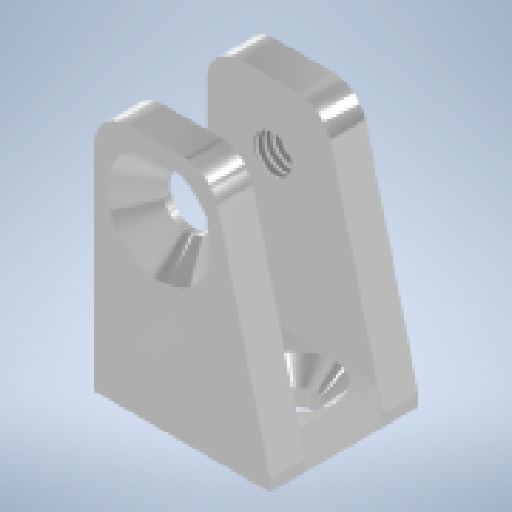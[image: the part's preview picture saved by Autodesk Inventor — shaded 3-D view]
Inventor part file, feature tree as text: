
AUTODESK INVENTOR PART (.ipt)
format: ipt  version: 2025 (Build 290162010, 162A)  size: 224,768 bytes
history: native  units: mm
features: sketch x5, hole x3, extrude x2, chamfer x2, fillet x1
ambient origin geometry x8: Origin, YZ Plane, XZ Plane, XY Plane, X Axis, Y Axis, Z Axis, Center Point
bodies: Volumenkörper1 (feature_tree)
feature tree (13):
  extrude  "Extrusion1"  Depth=3.0mm
  chamfer  "Fasen1"  Distance=21.0mm
  chamfer  "Fasen2"  Distance=20.0mm
  fillet  "Rundung1"  Radius=5.0mm
  hole  "Bohrung1"  [1 undecoded]
  extrude  "Extrusion2"  Depth=8.0mm
  hole  "Bohrung2"  [1 undecoded]
  hole  "Bohrung3"  [1 undecoded]
  sketch  "Skizze1"  dims[d0=15.0mm d1=3.0mm]
  sketch  "Skizze2"  dims[d2=3.0mm]
  sketch  "Skizze3"  dims[d3=6.6mm d5=21.0mm d6=0.0mm]
  sketch  "Skizze4"  dims[d7=3.0mm]
  sketch  "Skizze5"  dims[d8=3.242mm d9=8.0mm d10=9.0mm d11=14.0mm d12=90.0deg d13=11.8mm d14=20.594885mm d16=20.0mm d17=0.0mm d19=3.2mm d20=8.0mm d21=6.3mm d22=2.0mm d23=90.0deg d24=8.0mm d25=20.594885mm d26=4.3mm d27=8.0mm d28=4.0mm d29=2.0mm d30=90.0deg d31=5.0mm d32=20.594885mm d42=5.0mm d43=21.0mm d44=45.0deg d45=5.0mm d46=21.0mm d47=45.0deg d48=8.0mm d49=3.0mm d50=3.047619mm d51=4.0mm d52=0.5mm d53=0.872665mm d54=0.5mm d55=0.872665mm]
note: 3 required parameter values undecoded (feature->parameter linkage not recoverable at this tier; creation-order binding heuristic only, values carry confidence <= 0.55)
